# Revit family: Salon_CB-562_BIM
name_source: partatom
category: Arredi
units: mm (PartAtom-declared; Revit-internal decimal feet)

## family parameters
Attiva taglio nelle viste = No
Basato su piano di lavoro = No
Condiviso = No
Numero OmniClass = 23.40.20.00
Origine composizione di rendering = Geometria famiglia
Punto di calcolo locali = No
Sempre verticale = Sì
Taglio con vuoti quando caricato = No
Titolo OmniClass = General Furniture and Specialties

## types (1)
- CB-562
    BASE MATERIAL = BASSAM_FELLOWS_COMFORT_LEATHER_02067_BEIGE
    BIM BADGE = https://bim.archiproducts.com
    COLLECTION = Salon
    DEPTH = 724 mm  [stored 2.37533 ft]
    Descrizione = Sofa with down and feather topper
    FEET MATERIAL = BASSAM_FELLOWS_WALNUT_BLACK_OIL_W-BO
    HEIGHT = 692 mm
    MATERIAL DESCRIPTION = Multilayered plywood inner frame; seat support with a combination of foam and memory foam; arm and back in foam; seat and bolster cushions in feather and down.
    Modello = Salon Settee
    PRODUCT CODE = CB-562
    PRODUCT SHEET = https://www.archiproducts.com
    Produttore = BassamFellows
    Prospetto di default = 0 mm  [stored 0 ft]
    TECHNICAL SHEET = https://bassamfellows.com
    UPHOLSTERY MATERIAL = BASSAM_FELLOWS_COMFORT_LEATHER_02067_BEIGE
    URL = https://bassamfellows.com
    WIDTH = 1295 mm

note: [stored X ft] marks values corroborated as IEEE doubles in the binary element streams (Revit-internal decimal feet)

## geometry (parser evidence)
native form markers: Sweep x2
no freeform markers — native parametric forms only
